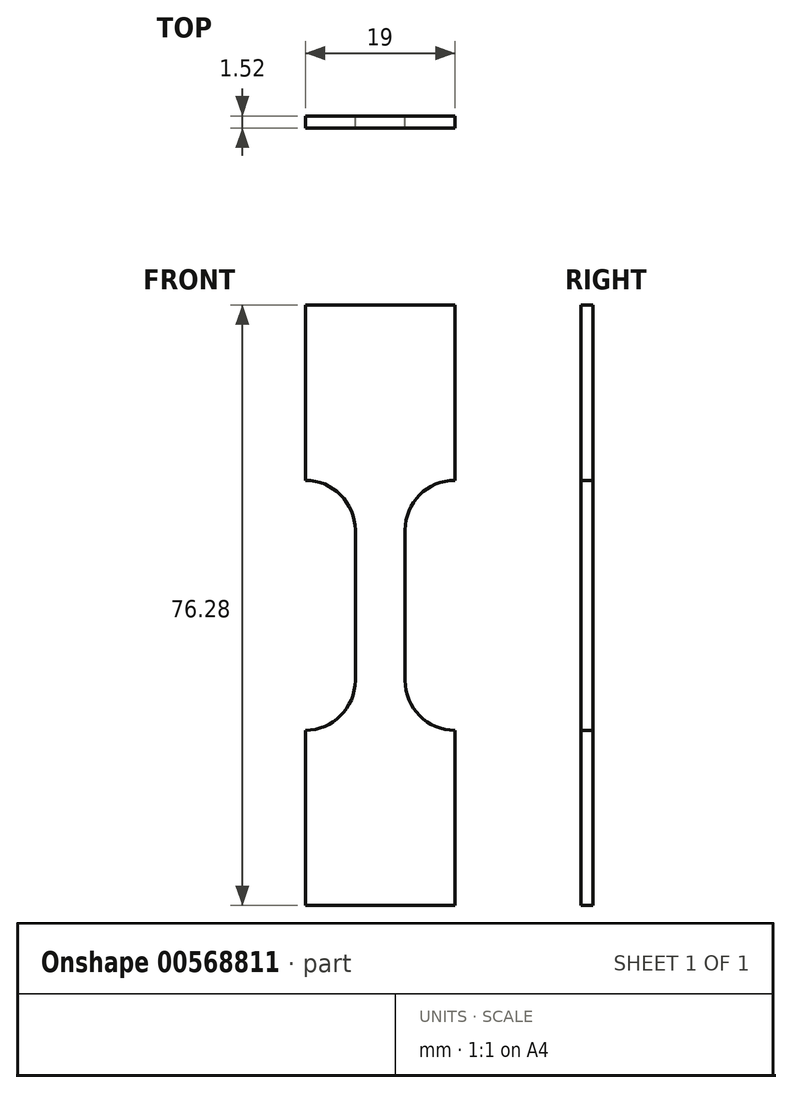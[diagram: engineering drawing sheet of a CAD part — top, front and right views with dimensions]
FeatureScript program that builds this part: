
annotation { "Feature Type Name" : "Feature", "Feature Type Description" : "" }
export const myFeature = defineFeature(function(context is Context, id is Id, definition is map)
    precondition{}
    {
        {
            var Q0;
            Q0=qCreatedBy(makeId("Front.planeOp"),FACE);
            var sketch = newSketch(context, id + "F0", { "sketchPlane" : qUnion([Q0])});
            skLineSegment(sketch, "E0", {"start": v(-3.16, 0) * mm, "end": v(-3.16, 9.54) * mm});
            skLineSegment(sketch, "E1", {"start": v(3.16, 0) * mm, "end": v(3.16, 9.54) * mm});
            skArc(sketch, "E2", {"start": v(-3.16, 9.54) * mm, "mid": v(-5.02, 14.02) * mm, "end": v(-9.5, 15.88) * mm});
            skArc(sketch, "E3", {"start": v(9.5, 15.88) * mm, "mid": v(5.02, 14.02) * mm, "end": v(3.16, 9.54) * mm});
            skLineSegment(sketch, "E4", {"start": v(-9.5, 15.88) * mm, "end": v(-9.5, 38.14) * mm});
            skLineSegment(sketch, "E5", {"start": v(9.5, 15.88) * mm, "end": v(9.5, 38.14) * mm});
            skLineSegment(sketch, "E6", {"start": v(-9.5, 38.14) * mm, "end": v(9.5, 38.14) * mm});
            skLineSegment(sketch, "E7.MirrorCS", {"start": v(-9.5, -38.14) * mm, "end": v(9.5, -38.14) * mm});
            skLineSegment(sketch, "E8.MirrorCS", {"start": v(-9.5, -15.88) * mm, "end": v(-9.5, -38.14) * mm});
            skLineSegment(sketch, "E9.MirrorCS", {"start": v(9.5, -15.88) * mm, "end": v(9.5, -38.14) * mm});
            skArc(sketch, "E10.MirrorCS", {"start": v(9.5, -15.88) * mm, "mid": v(5.02, -14.02) * mm, "end": v(3.16, -9.54) * mm});
            skArc(sketch, "E11.MirrorCS", {"start": v(-3.16, -9.54) * mm, "mid": v(-5.02, -14.02) * mm, "end": v(-9.5, -15.88) * mm});
            skLineSegment(sketch, "E12.MirrorCS", {"start": v(3.16, 0) * mm, "end": v(3.16, -9.54) * mm});
            skLineSegment(sketch, "E13.MirrorCS", {"start": v(-3.16, 0) * mm, "end": v(-3.16, -9.54) * mm});
            skSolve(sketch);
        }
        {
            var Q0;
            Q0=makeQuery(id+"F0.imprint","IMPRINT",FACE,{"disambiguationData":[TD([[makeQuery(id+"F0.imprint","IMPRINT",EDGE,{"derivedFrom":sQuery(id+"F0.wireOp",EDGE,"E0")}),-1.0]])]});
            extrude(context, id + "F1", {"entities" : qUnion([Q0]), "depth" : 1.52 * mm, "offsetDistance" : 25 * mm});
        }
    });
